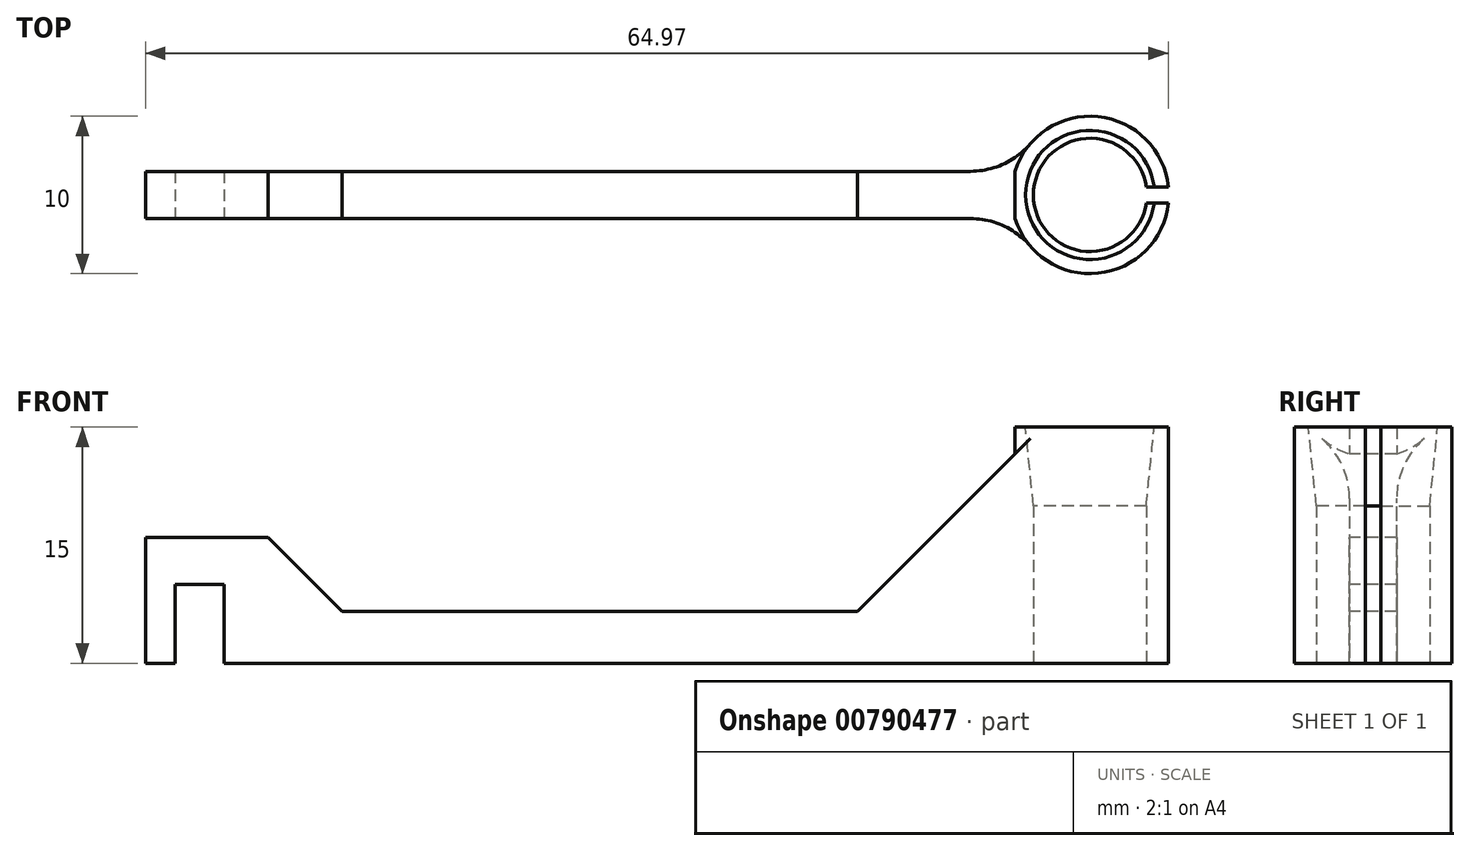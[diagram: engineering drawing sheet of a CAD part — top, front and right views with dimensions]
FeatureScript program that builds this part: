
annotation { "Feature Type Name" : "Feature", "Feature Type Description" : "" }
export const myFeature = defineFeature(function(context is Context, id is Id, definition is map)
    precondition{}
    {
        {
            var Q0;
            Q0=qCreatedBy(makeId("Top.planeOp"),FACE);
            var sketch = newSketch(context, id + "F0", { "sketchPlane" : qUnion([Q0])});
            skLineSegment(sketch, "E0.bottom", {"start": v(55.23, 1.5) * mm, "end": v(0, 1.5) * mm});
            skLineSegment(sketch, "E0.top", {"start": v(55.23, -1.5) * mm, "end": v(0, -1.5) * mm});
            skPoint(sketch, "E0.middle", {"position": v(0, 0) * mm});
            skLineSegment(sketch, "E1", {"start": v(0, 1.5) * mm, "end": v(0, -1.5) * mm});
            skPoint(sketch, "E1.endSnap0", {"position": v(0, -1.5) * mm});
            skPoint(sketch, "E2.orphan", {"position": v(0, 5.95) * mm});
            skPoint(sketch, "E3.orphan", {"position": v(0, -6.91) * mm});
            skPoint(sketch, "E0.right.end.orphan", {"position": v(-60, -1.5) * mm});
            skPoint(sketch, "E0.right.start.orphan", {"position": v(-60, 1.5) * mm});
            skPoint(sketch, "E4", {"position": v(60, 0) * mm});
            skArc(sketch, "E5", {"start": v(63.57, 0.5) * mm, "mid": v(56.4, 0) * mm, "end": v(63.57, -0.5) * mm});
            skArc(sketch, "E6", {"start": v(55.23, -1.5) * mm, "mid": v(60.51, -4.97) * mm, "end": v(64.97, -0.5) * mm});
            skPoint(sketch, "E7.orphan", {"position": v(60, -1.5) * mm});
            skPoint(sketch, "E8.orphan", {"position": v(60, 1.5) * mm});
            skLineSegment(sketch, "E9.bottom", {"start": v(64.97, 0.5) * mm, "end": v(63.57, 0.5) * mm});
            skLineSegment(sketch, "E9.top", {"start": v(64.97, -0.5) * mm, "end": v(63.57, -0.5) * mm});
            skPoint(sketch, "E9.middle", {"position": v(63.6, 0) * mm});
            skArc(sketch, "E10.trimOffspring", {"start": v(64.97, 0.5) * mm, "mid": v(60.51, 4.97) * mm, "end": v(55.23, 1.5) * mm});
            skPoint(sketch, "E9.left.end.orphan", {"position": v(66.51, -0.5) * mm});
            skPoint(sketch, "E9.left.start.orphan", {"position": v(66.51, 0.5) * mm});
            skPoint(sketch, "E9.right.end.orphan", {"position": v(60.69, -0.5) * mm});
            skPoint(sketch, "E9.right.start.orphan", {"position": v(60.69, 0.5) * mm});
            skSolve(sketch);
        }
        {
            var Q0;
            Q0=qSketchRegion(id+"F0",true);
            extrude(context, id + "F1", {"entities" : qUnion([Q0]), "depth" : 15 * mm, "offsetDistance" : 25 * mm});
        }
        {
            var Q0;
            Q0=makeQuery(id+"F1.opExtrude","SWEPT_FACE",FACE,{"disambiguationData":[OSD([sQuery(id+"F0.wireOp",EDGE,"E0.top")])]});
            var sketch = newSketch(context, id + "F2", { "sketchPlane" : qUnion([Q0])});
            skLineSegment(sketch, "E11", {"start": v(55.23, 3.3) * mm, "end": v(55.23, 15) * mm});
            skLineSegment(sketch, "E12", {"start": v(55.23, 15) * mm, "end": v(0, 15) * mm});
            skLineSegment(sketch, "E13", {"start": v(0, 15) * mm, "end": v(0, 3.3) * mm});
            skLineSegment(sketch, "E14.bottom", {"start": v(1.9, 0) * mm, "end": v(5, 0) * mm});
            skLineSegment(sketch, "E14.top", {"start": v(0, 8) * mm, "end": v(7.5, 8) * mm});
            skLineSegment(sketch, "E14.right", {"start": v(7.5, 3.3) * mm, "end": v(7.5, 8) * mm});
            skLineSegment(sketch, "E15", {"start": v(1.9, 0) * mm, "end": v(1.9, 5) * mm});
            skLineSegment(sketch, "E16", {"start": v(1.9, 5) * mm, "end": v(5, 5) * mm});
            skLineSegment(sketch, "E17", {"start": v(5, 5) * mm, "end": v(5, 0) * mm});
            skLineSegment(sketch, "E18.trimOffspring", {"start": v(7.5, 3.3) * mm, "end": v(55.23, 3.3) * mm});
            skPoint(sketch, "E14.left.start.orphan", {"position": v(0, 0) * mm});
            skSolve(sketch);
        }
        {
            var Q0;
            Q0=qSketchRegion(id+"F2",true);
            extrude(context, id + "F3", {"entities" : qUnion([Q0]), "operationType" : NewBodyOperationType.REMOVE, "oppositeDirection" : true, "depth" : 25 * mm, "offsetDistance" : 25 * mm});
        }
        {
            var Q0;
            Q0=makeQuery(id+"F3.boolean.opBoolean","COPY",EDGE,{"derivedFrom":makeQuery(id+"F3.opExtrude","SWEPT_EDGE",EDGE,{"disambiguationData":[OSD([sQuery(id+"F0.wireOp",EDGE,"E0.top"),sQuery(id+"F0.wireOp",EDGE,"E6"),sQuery(id+"F2.wireOp",EDGE,"E11"),sQuery(id+"F2.wireOp",EDGE,"E18.trimOffspring")])]})});
            chamfer(context, id + "F4", {"entities" : qUnion([Q0]), "width" : 10 * mm, "tangentPropagation" : true});
        }
        {
            var Q0;
            Q0=makeQuery(id+"F3.boolean.opBoolean","COPY",EDGE,{"derivedFrom":makeQuery(id+"F3.opExtrude","SWEPT_EDGE",EDGE,{"disambiguationData":[OSD([sQuery(id+"F2.wireOp",EDGE,"E14.right"),sQuery(id+"F2.wireOp",EDGE,"E18.trimOffspring")])]})});
            chamfer(context, id + "F5", {"entities" : qUnion([Q0]), "width" : 5 * mm, "tangentPropagation" : true});
        }
        {
            var Q0;
            Q0=makeQuery(id+"F3.boolean.opBoolean","SPLIT",EDGE,{"derivedFrom":makeQuery(id+"F1.opExtrude","SWEPT_EDGE",EDGE,{"disambiguationData":[OSD([sQuery(id+"F0.wireOp",EDGE,"E0.top"),sQuery(id+"F0.wireOp",EDGE,"E6")])]})});
            var Q1;
            {var subQ0=sQuery(id+"F0.wireOp",EDGE,"E0.bottom");var subQ1=sQuery(id+"F0.wireOp",EDGE,"E10.trimOffspring");Q1=makeQuery(id+"F3.boolean.opBoolean","SPLIT",EDGE,{"disambiguationData":[topologyDisambiguationEdgeConnected([makeQuery(id+"F1.opExtrude","SWEPT_FACE",FACE,{"disambiguationData":[OSD([subQ0])]})])],"derivedFrom":makeQuery(id+"F1.opExtrude","SWEPT_EDGE",EDGE,{"disambiguationData":[OSD([subQ0,subQ1])]})});}
            fillet(context, id + "F6", {"entities" : qUnion([Q0, Q1]), "radius" : 5 * mm, "tangentPropagation" : true, "allowEdgeOverflow" : false});
        }
        {
            var Q0;
            Q0=makeQuery(id+"F1.opExtrude","CAP_EDGE",EDGE,{"disambiguationData":[OSD([sQuery(id+"F0.wireOp",EDGE,"E5")])],"isStart":false});
            chamfer(context, id + "F7", {"entities" : qUnion([Q0]), "chamferType" : ChamferType.TWO_OFFSETS, "width1" : 5 * mm, "oppositeDirection" : false, "width2" : .5 * mm, "tangentPropagation" : true});
        }
    });
